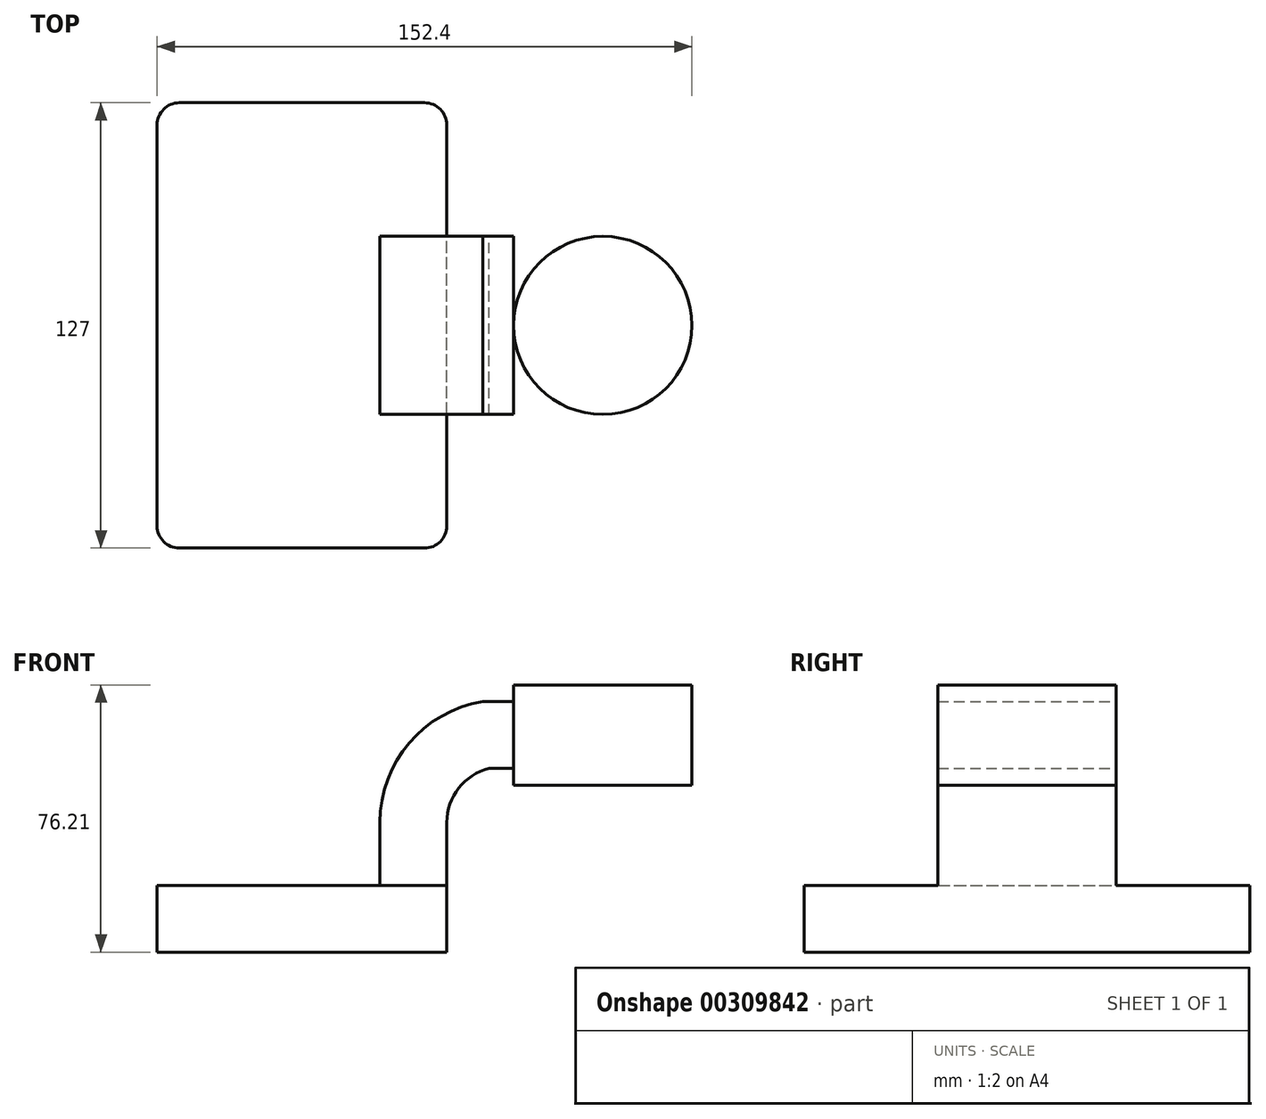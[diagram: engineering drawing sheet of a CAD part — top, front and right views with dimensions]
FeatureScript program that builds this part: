
annotation { "Feature Type Name" : "Feature", "Feature Type Description" : "" }
export const myFeature = defineFeature(function(context is Context, id is Id, definition is map)
    precondition{}
    {
        {
            var Q0;
            Q0=qCreatedBy(makeId("Front.planeOp"),FACE);
            var sketch = newSketch(context, id + "F0", { "sketchPlane" : qUnion([Q0])});
            skLineSegment(sketch, "E0.bottom", {"start": v(-41.28, 9.52) * mm, "end": v(41.28, 9.52) * mm});
            skLineSegment(sketch, "E0.top", {"start": v(-41.28, -9.52) * mm, "end": v(41.28, -9.52) * mm});
            skLineSegment(sketch, "E0.left", {"start": v(-41.28, 9.52) * mm, "end": v(-41.28, -9.52) * mm});
            skLineSegment(sketch, "E0.right", {"start": v(41.28, 9.52) * mm, "end": v(41.28, -9.52) * mm});
            skPoint(sketch, "E0.middle", {"position": v(0, 0) * mm});
            skLineSegment(sketch, "E1.bottom", {"start": v(111.12, 38.1) * mm, "end": v(60.32, 38.1) * mm});
            skLineSegment(sketch, "E1.top", {"start": v(111.12, 66.68) * mm, "end": v(60.32, 66.68) * mm});
            skLineSegment(sketch, "E1.left", {"start": v(111.12, 38.1) * mm, "end": v(111.12, 66.68) * mm});
            skLineSegment(sketch, "E1.right", {"start": v(60.32, 38.1) * mm, "end": v(60.32, 66.68) * mm});
            skPoint(sketch, "E1.middle", {"position": v(85.72, 52.39) * mm});
            skLineSegment(sketch, "E2", {"start": v(41.28, 9.52) * mm, "end": v(41.28, 27.44) * mm});
            skArc(sketch, "E3", {"start": v(41.28, 27.44) * mm, "mid": v(44.66, 37.24) * mm, "end": v(53.37, 42.86) * mm});
            skLineSegment(sketch, "E4", {"start": v(53.37, 42.86) * mm, "end": v(85.72, 42.86) * mm});
            skLineSegment(sketch, "E5.0", {"start": v(51.52, 61.91) * mm, "end": v(85.72, 61.91) * mm});
            skArc(sketch, "E5.1", {"start": v(22.23, 27.44) * mm, "mid": v(30.54, 50.06) * mm, "end": v(51.52, 61.91) * mm});
            skLineSegment(sketch, "E5.2", {"start": v(22.23, 9.52) * mm, "end": v(22.23, 27.44) * mm});
            skLineSegment(sketch, "E6", {"start": v(85.72, 38.1) * mm, "end": v(85.72, 66.68) * mm});
            skFitSpline(sketch, "E7", {"points": [v(-41.28, 9.52) * mm, v(57.03, 61.91) * mm], "startDerivative": vector(95.21, 133.74) * mm, "endDerivative": vector(122.1, -8.53) * mm});
            skSolve(sketch);
        }
        {
            var Q0;
            Q0=makeQuery(id+"F0.imprint","IMPRINT",FACE,{"disambiguationData":[TD([[makeQuery(id+"F0.imprint","IMPRINT",EDGE,{"derivedFrom":sQuery(id+"F0.wireOp",EDGE,"E0.top")}),1.0]])]});
            extrude(context, id + "F1", {"entities" : qUnion([Q0]), "endBound" : BoundingType.SYMMETRIC, "depth" : 127 * mm});
        }
        {
            var Q0;
            {var subQ1=sQuery(id+"F0.wireOp",EDGE,"E2");Q0=makeQuery(id+"F0.imprint","IMPRINT",FACE,{"disambiguationData":[TD([[makeQuery(id+"F0.imprint","IMPRINT",EDGE,{"derivedFrom":subQ1}),1.0]])]});}
            extrude(context, id + "F2", {"entities" : qUnion([Q0]), "operationType" : NewBodyOperationType.ADD, "endBound" : BoundingType.SYMMETRIC, "depth" : 50.8 * mm});
        }
        {
            var Q0;
            {var subQ1=sQuery(id+"F0.wireOp",EDGE,"E5.1");Q0=makeQuery(id+"F0.imprint","IMPRINT",FACE,{"disambiguationData":[TD([[makeQuery(id+"F0.imprint","IMPRINT",EDGE,{"derivedFrom":subQ1}),1.0]])]});}
            extrude(context, id + "F3", {"entities" : qUnion([Q0]), "operationType" : NewBodyOperationType.ADD, "endBound" : BoundingType.SYMMETRIC, "depth" : 12.7 * mm});
        }
        {
            var Q0;
            {var subQ0=sQuery(id+"F0.wireOp",EDGE,"E1.left");Q0=makeQuery(id+"F0.imprint","IMPRINT",FACE,{"disambiguationData":[TD([[makeQuery(id+"F0.imprint","IMPRINT",EDGE,{"derivedFrom":subQ0}),1.0]])]});}
            var Q1;
            Q1=sQuery(id+"F0.wireOp",EDGE,"E6");
            revolve(context, id + "F4", {"operationType" : NewBodyOperationType.ADD, "entities" : qUnion([Q0]), "axis" : qUnion([Q1]), "revolveType" : RevolveType.FULL});
        }
        {
            var Q0;
            Q0=makeQuery(id+"F1.opExtrude","CAP_EDGE",EDGE,{"disambiguationData":[OSD([sQuery(id+"F0.wireOp",EDGE,"E0.right")])],"isStart":false});
            var Q1;
            Q1=makeQuery(id+"F1.opExtrude","CAP_EDGE",EDGE,{"disambiguationData":[OSD([sQuery(id+"F0.wireOp",EDGE,"E0.left")])],"isStart":false});
            var Q2;
            Q2=makeQuery(id+"F1.opExtrude","CAP_EDGE",EDGE,{"disambiguationData":[OSD([sQuery(id+"F0.wireOp",EDGE,"E0.right")])],"isStart":true});
            var Q3;
            Q3=makeQuery(id+"F1.opExtrude","CAP_EDGE",EDGE,{"disambiguationData":[OSD([sQuery(id+"F0.wireOp",EDGE,"E0.left")])],"isStart":true});
            fillet(context, id + "F5", {"entities" : qUnion([Q0, Q1, Q2, Q3]), "radius" : 6.35 * mm, "tangentPropagation" : true, "allowEdgeOverflow" : false});
        }
    });
